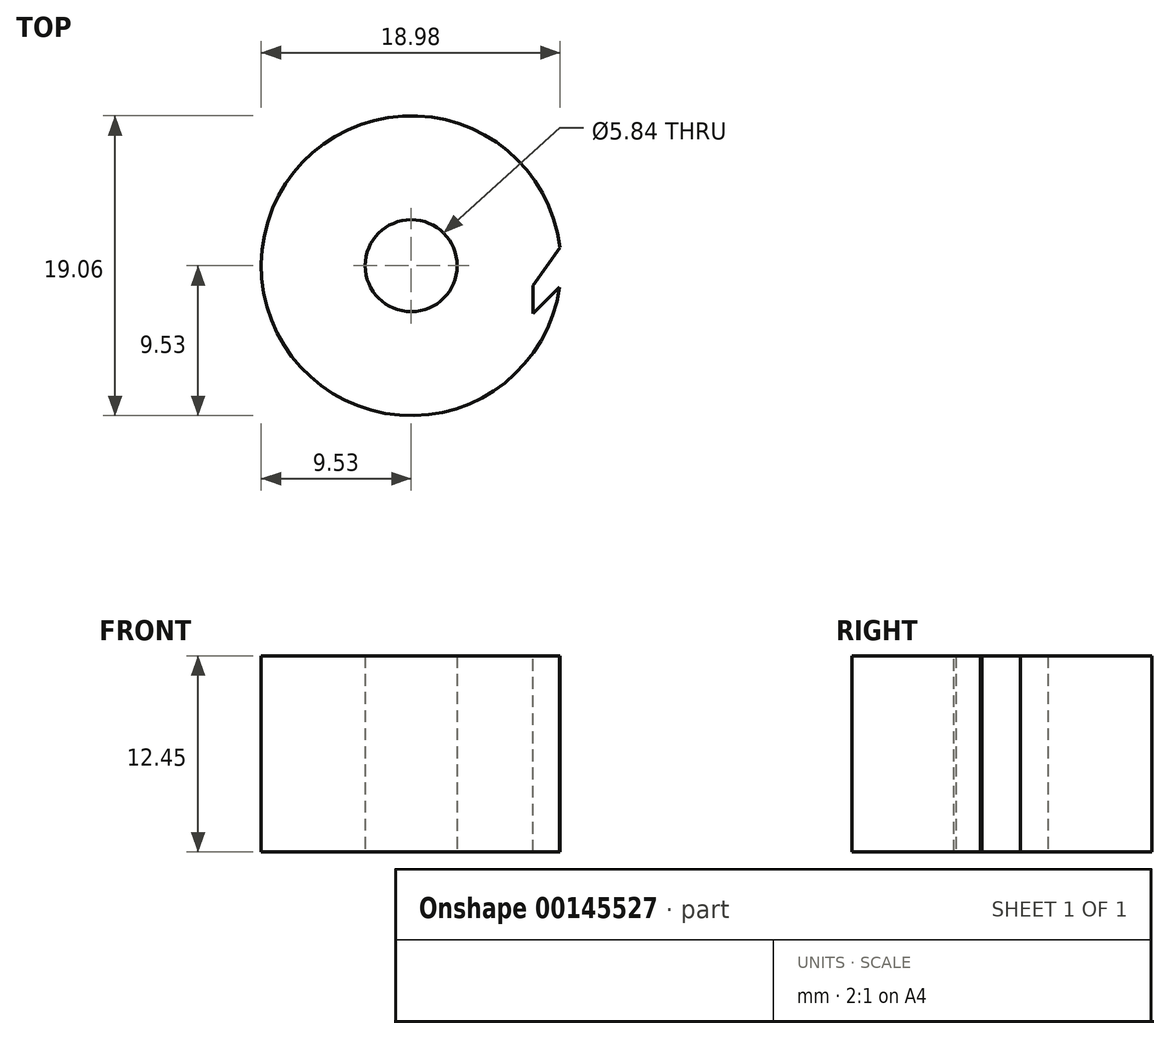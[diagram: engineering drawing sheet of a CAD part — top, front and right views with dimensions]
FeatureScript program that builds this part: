
annotation { "Feature Type Name" : "Feature", "Feature Type Description" : "" }
export const myFeature = defineFeature(function(context is Context, id is Id, definition is map)
    precondition{}
    {
        {
            var Q0;
            Q0=qCreatedBy(makeId("Right.planeOp"),FACE);
            cPlane(context, id + "F0", {"entities" : qUnion([Q0]), "cplaneType" : CPlaneType.OFFSET, "offset" : 2.92 * mm, "width" : 152.4 * mm, "height" : 152.4 * mm});
        }
        {
            var Q0;
            Q0=qCreatedBy(makeId("Right.planeOp"),FACE);
            cPlane(context, id + "F1", {"entities" : qUnion([Q0]), "cplaneType" : CPlaneType.OFFSET, "offset" : 9.52 * mm, "width" : 152.4 * mm, "height" : 152.4 * mm});
        }
        {
            var Q0;
            Q0=qCreatedBy(makeId("Top.planeOp"),FACE);
            var sketch = newSketch(context, id + "F2", { "sketchPlane" : qUnion([Q0])});
            skCircle(sketch, "E0", {"center": v(0, 0) * mm, "radius": 9.53 * mm});
            skCircle(sketch, "E1", {"center": v(0, 0) * mm, "radius": 2.92 * mm});
            skSolve(sketch);
        }
        {
            var Q0;
            Q0 = qSketchRegion(id + "F2", true);
            extrude(context, id + "F3", {"entities" : qUnion([Q0]), "depth" : 12.45 * mm});
        }
        {
            var Q0;
            Q0=makeQuery(id+"F3.opExtrude","CAP_FACE",FACE,{"disambiguationData":[OSD([sQuery(id+"F2.wireOp",EDGE,"E0"),sQuery(id+"F2.wireOp",EDGE,"E1")])],"isStart":false});
            var sketch = newSketch(context, id + "F4", { "sketchPlane" : qUnion([Q0])});
            skLineSegment(sketch, "E2", {"start": v(-1.03, 0) * mm, "end": v(12.85, 0) * mm, "construction": true});
            skLineSegment(sketch, "E3", {"start": v(9.53, 1.27) * mm, "end": v(9.53, -1.27) * mm});
            skLineSegment(sketch, "E4", {"start": v(9.53, -1.27) * mm, "end": v(7.75, -3.05) * mm});
            skLineSegment(sketch, "E5", {"start": v(7.75, -3.05) * mm, "end": v(7.75, -1.27) * mm});
            skLineSegment(sketch, "E6", {"start": v(7.75, -1.27) * mm, "end": v(9.53, 1.27) * mm});
            skSolve(sketch);
        }
        {
            var Q0;
            Q0 = qSketchRegion(id + "F4", true);
            var Q1;
            Q1=makeQuery(id+"F3.opExtrude","CAP_FACE",FACE,{"disambiguationData":[OSD([sQuery(id+"F2.wireOp",EDGE,"E0"),sQuery(id+"F2.wireOp",EDGE,"E1")])],"isStart":true});
            extrude(context, id + "F5", {"entities" : qUnion([Q0]), "operationType" : NewBodyOperationType.REMOVE, "endBound" : BoundingType.UP_TO_SURFACE, "oppositeDirection" : true, "endBoundEntityFace" : qUnion([Q1]), "depth" : 25.4 * mm});
        }
    });
